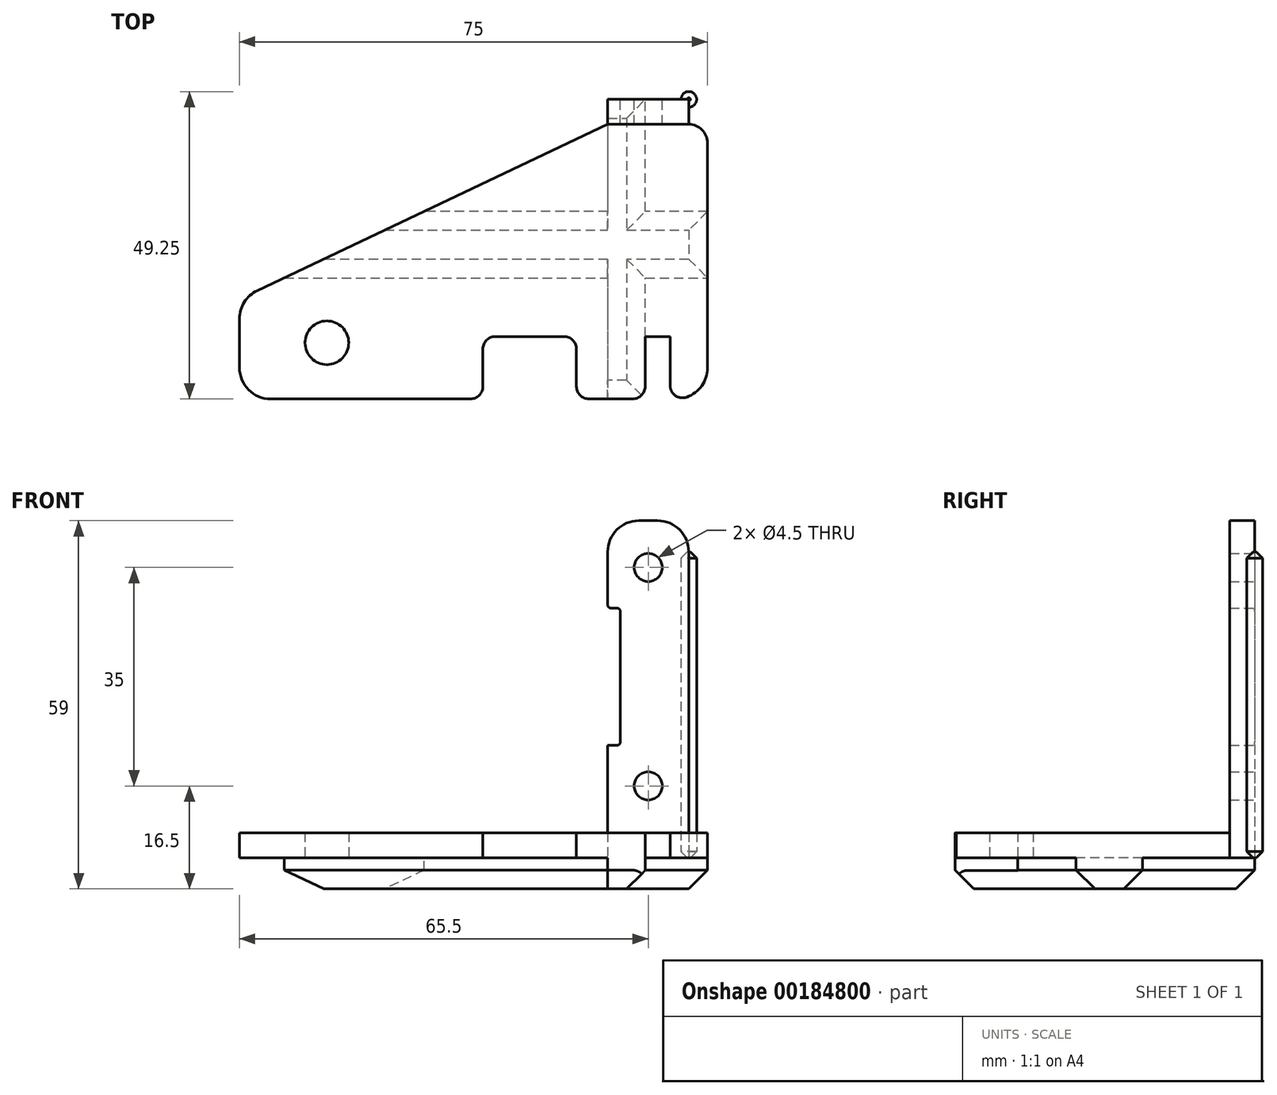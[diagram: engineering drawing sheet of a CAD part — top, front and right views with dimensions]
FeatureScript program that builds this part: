
annotation { "Feature Type Name" : "Feature", "Feature Type Description" : "" }
export const myFeature = defineFeature(function(context is Context, id is Id, definition is map)
    precondition{}
    {
        {
            var Q0;
            Q0=qCreatedBy(makeId("Top.planeOp"),FACE);
            var sketch = newSketch(context, id + "F0", { "sketchPlane" : qUnion([Q0])});
            skLineSegment(sketch, "E0.bottom", {"start": v(5, 0) * mm, "end": v(70, 0) * mm});
            skLineSegment(sketch, "E0.top", {"start": v(59, 44) * mm, "end": v(72, 44) * mm});
            skLineSegment(sketch, "E0.left", {"start": v(0, 5) * mm, "end": v(0, 12.84) * mm});
            skLineSegment(sketch, "E0.right", {"start": v(75, 5) * mm, "end": v(75, 41) * mm});
            skCircle(sketch, "E1", {"center": v(14, 9) * mm, "radius": 3.5 * mm});
            skLineSegment(sketch, "E2.bottom", {"start": v(69, 0) * mm, "end": v(65, 0) * mm});
            skLineSegment(sketch, "E2.top", {"start": v(69, 10) * mm, "end": v(65, 10) * mm});
            skLineSegment(sketch, "E2.left", {"start": v(69, 0) * mm, "end": v(69, 10) * mm});
            skLineSegment(sketch, "E2.right", {"start": v(65, 0) * mm, "end": v(65, 10) * mm});
            skLineSegment(sketch, "E3.bottom", {"start": v(72, 48) * mm, "end": v(59, 48) * mm});
            skLineSegment(sketch, "E3.top", {"start": v(72, 44) * mm, "end": v(59, 44) * mm});
            skLineSegment(sketch, "E3.left", {"start": v(72, 48) * mm, "end": v(72, 44) * mm});
            skLineSegment(sketch, "E3.right", {"start": v(59, 48) * mm, "end": v(59, 44) * mm});
            skLineSegment(sketch, "E4", {"start": v(59, 44) * mm, "end": v(2.86, 17.36) * mm});
            skPoint(sketch, "E5.visualSharp", {"position": v(75, 44) * mm});
            skArc(sketch, "E5.filletArc", {"start": v(75, 41) * mm, "mid": v(74.12, 43.12) * mm, "end": v(72, 44) * mm});
            skPoint(sketch, "E6.visualSharp", {"position": v(75, 0) * mm});
            skArc(sketch, "E6.filletArc", {"start": v(70, 0) * mm, "mid": v(73.54, 1.46) * mm, "end": v(75, 5) * mm});
            skPoint(sketch, "E7.visualSharp", {"position": v(0, 16) * mm});
            skArc(sketch, "E7.filletArc", {"start": v(2.86, 17.36) * mm, "mid": v(0.77, 15.51) * mm, "end": v(0, 12.84) * mm});
            skPoint(sketch, "E8.visualSharp", {"position": v(0, 0) * mm});
            skArc(sketch, "E8.filletArc", {"start": v(0, 5) * mm, "mid": v(1.46, 1.46) * mm, "end": v(5, 0) * mm});
            skLineSegment(sketch, "E9.bottom", {"start": v(39, 0) * mm, "end": v(54, 0) * mm});
            skLineSegment(sketch, "E9.top", {"start": v(39, 10) * mm, "end": v(54, 10) * mm});
            skLineSegment(sketch, "E9.left", {"start": v(39, 0) * mm, "end": v(39, 10) * mm});
            skLineSegment(sketch, "E9.right", {"start": v(54, 0) * mm, "end": v(54, 10) * mm});
            skSolve(sketch);
        }
        {
            var Q0;
            Q0=makeQuery(id+"F0.imprint","IMPRINT",FACE,{"disambiguationData":[TD([[makeQuery(id+"F0.imprint","IMPRINT",EDGE,{"derivedFrom":sQuery(id+"F0.wireOp",EDGE,"E0.left")}),-1.0]])]});
            extrude(context, id + "F1", {"entities" : qUnion([Q0]), "depth" : 4 * mm});
        }
        {
            var Q0;
            Q0=makeQuery(id+"F0.imprint","IMPRINT",FACE,{"disambiguationData":[TD([[makeQuery(id+"F0.imprint","IMPRINT",EDGE,{"derivedFrom":sQuery(id+"F0.wireOp",EDGE,"E3.bottom")}),1.0]])]});
            extrude(context, id + "F2", {"entities" : qUnion([Q0]), "operationType" : NewBodyOperationType.ADD, "depth" : 54 * mm});
        }
        {
            var Q0;
            Q0=makeQuery(id+"F2.opExtrude","CAP_EDGE",EDGE,{"disambiguationData":[OSD([sQuery(id+"F0.wireOp",EDGE,"E3.left")])],"isStart":false});
            var Q1;
            Q1=makeQuery(id+"F2.opExtrude","CAP_EDGE",EDGE,{"disambiguationData":[OSD([sQuery(id+"F0.wireOp",EDGE,"E3.right")])],"isStart":false});
            fillet(context, id + "F3", {"entities" : qUnion([Q0, Q1]), "radius" : 5 * mm, "tangentPropagation" : true, "allowEdgeOverflow" : false});
        }
        {
            var Q0;
            Q0=makeQuery(id+"F0.imprint","IMPRINT",FACE,{"disambiguationData":[TD([[makeQuery(id+"F0.imprint","IMPRINT",EDGE,{"derivedFrom":sQuery(id+"F0.wireOp",EDGE,"E0.left")}),-1.0]])]});
            var sketch = newSketch(context, id + "F4", { "sketchPlane" : qUnion([Q0])});
            skLineSegment(sketch, "E10", {"start": v(7.19, 19.4) * mm, "end": v(59, 19.4) * mm});
            skLineSegment(sketch, "E11", {"start": v(75.05, 19.4) * mm, "end": v(75.05, 30.04) * mm});
            skLineSegment(sketch, "E12", {"start": v(75.05, 30.04) * mm, "end": v(65.04, 30.04) * mm});
            skLineSegment(sketch, "E13", {"start": v(29.59, 30.04) * mm, "end": v(7.19, 19.4) * mm});
            skLineSegment(sketch, "E14", {"start": v(59, 48) * mm, "end": v(59, 30.04) * mm});
            skLineSegment(sketch, "E15", {"start": v(59, 0) * mm, "end": v(65.04, 0) * mm});
            skLineSegment(sketch, "E16", {"start": v(65.04, 0) * mm, "end": v(65.04, 19.4) * mm});
            skLineSegment(sketch, "E17", {"start": v(65.04, 48) * mm, "end": v(59, 48) * mm});
            skLineSegment(sketch, "E18.trimOffspring", {"start": v(59, 19.4) * mm, "end": v(59, 0) * mm});
            skLineSegment(sketch, "E19.trimOffspring", {"start": v(65.04, 30.04) * mm, "end": v(65.04, 48) * mm});
            skLineSegment(sketch, "E20.trimOffspring", {"start": v(65.04, 19.4) * mm, "end": v(75.05, 19.4) * mm});
            skLineSegment(sketch, "E21.trimOffspring", {"start": v(59, 30.04) * mm, "end": v(29.59, 30.04) * mm});
            skCircle(sketch, "E22", {"center": v(72, 48) * mm, "radius": 1.25 * mm});
            skSolve(sketch);
        }
        {
            var Q0;
            {var subQ24=sQuery(id+"F4.wireOp",EDGE,"E10");Q0=makeQuery(id+"F4.imprint","IMPRINT",FACE,{"disambiguationData":[TD([[makeQuery(id+"F4.imprint","IMPRINT",EDGE,{"derivedFrom":subQ24}),1.0]])]});}
            var Q1;
            {var subQ0=sQuery(id+"F4.wireOp",EDGE,"E17");Q1=makeQuery(id+"F4.imprint","IMPRINT",FACE,{"disambiguationData":[TD([[makeQuery(id+"F4.imprint","IMPRINT",EDGE,{"derivedFrom":subQ0}),1.0]])]});}
            extrude(context, id + "F5", {"entities" : qUnion([Q0, Q1]), "operationType" : NewBodyOperationType.ADD, "oppositeDirection" : true, "depth" : 5 * mm});
        }
        {
            var Q0;
            Q0=makeQuery(id+"F5.opExtrude","CAP_EDGE",EDGE,{"disambiguationData":[OSD([sQuery(id+"F4.wireOp",EDGE,"E17")])],"isStart":false});
            var Q1;
            Q1=makeQuery(id+"F5.opExtrude","CAP_EDGE",EDGE,{"disambiguationData":[OSD([sQuery(id+"F4.wireOp",EDGE,"E15")])],"isStart":false});
            var Q2;
            Q2=makeQuery(id+"F5.opExtrude","CAP_EDGE",EDGE,{"disambiguationData":[OSD([sQuery(id+"F0.wireOp",EDGE,"E0.right")])],"isStart":false});
            var Q3;
            Q3=makeQuery(id+"F5.opExtrude","CAP_EDGE",EDGE,{"disambiguationData":[OSD([sQuery(id+"F4.wireOp",EDGE,"E12")])],"isStart":false});
            var Q4;
            Q4=makeQuery(id+"F5.opExtrude","CAP_EDGE",EDGE,{"disambiguationData":[OSD([sQuery(id+"F4.wireOp",EDGE,"E20.trimOffspring")])],"isStart":false});
            var Q5;
            Q5=makeQuery(id+"F5.opExtrude","CAP_EDGE",EDGE,{"disambiguationData":[OSD([sQuery(id+"F4.wireOp",EDGE,"E19.trimOffspring")])],"isStart":false});
            var Q6;
            Q6=makeQuery(id+"F5.opExtrude","CAP_EDGE",EDGE,{"disambiguationData":[OSD([sQuery(id+"F4.wireOp",EDGE,"E21.trimOffspring")])],"isStart":false});
            var Q7;
            Q7=makeQuery(id+"F5.opExtrude","CAP_EDGE",EDGE,{"disambiguationData":[OSD([sQuery(id+"F0.wireOp",EDGE,"E4")])],"isStart":false});
            var Q8;
            Q8=makeQuery(id+"F5.opExtrude","CAP_EDGE",EDGE,{"disambiguationData":[OSD([sQuery(id+"F4.wireOp",EDGE,"E10")])],"isStart":false});
            var Q9;
            Q9=makeQuery(id+"F5.opExtrude","CAP_EDGE",EDGE,{"disambiguationData":[OSD([sQuery(id+"F4.wireOp",EDGE,"E16")])],"isStart":false});
            chamfer(context, id + "F6", {"entities" : qUnion([Q0, Q1, Q2, Q3, Q4, Q5, Q6, Q7, Q8, Q9]), "width" : 3 * mm, "tangentPropagation" : true});
        }
        {
            var Q0;
            Q0=makeQuery(id+"F4.imprint","IMPRINT",FACE,{"disambiguationData":[TD([[makeQuery(id+"F4.imprint","IMPRINT",EDGE,{"derivedFrom":sQuery(id+"F4.wireOp",EDGE,"E22")}),1.0]])]});
            extrude(context, id + "F7", {"entities" : qUnion([Q0]), "operationType" : NewBodyOperationType.ADD, "depth" : 49 * mm});
        }
        {
            var Q0;
            Q0=makeQuery(id+"F7.opExtrude","CAP_EDGE",EDGE,{"disambiguationData":[OSD([sQuery(id+"F4.wireOp",EDGE,"E22")])],"isStart":false});
            chamfer(context, id + "F8", {"entities" : qUnion([Q0]), "width" : 1 * mm, "tangentPropagation" : true});
        }
        {
            var Q0;
            Q0=makeQuery(id+"F7.opExtrude","CAP_EDGE",EDGE,{"disambiguationData":[OSD([sQuery(id+"F4.wireOp",EDGE,"E22")])],"isStart":true});
            chamfer(context, id + "F9", {"entities" : qUnion([Q0]), "width" : 1 * mm, "tangentPropagation" : true});
        }
        {
            var Q0;
            Q0=makeQuery(id+"F5.boolean.opBoolean","MERGE",FACE,{"derivedFrom":[makeQuery(id+"F2.opExtrude","SWEPT_FACE",FACE,{"disambiguationData":[OSD([sQuery(id+"F0.wireOp",EDGE,"E3.bottom")])]}),makeQuery(id+"F5.opExtrude","SWEPT_FACE",FACE,{"disambiguationData":[OSD([sQuery(id+"F4.wireOp",EDGE,"E17")])]})]});
            var sketch = newSketch(context, id + "F10", { "sketchPlane" : qUnion([Q0])});
            skCircle(sketch, "E23", {"center": v(-65.5, 46.5) * mm, "radius": 2.25 * mm});
            skCircle(sketch, "E24", {"center": v(-65.5, 11.5) * mm, "radius": 2.25 * mm});
            skSolve(sketch);
        }
        {
            var Q0;
            Q0=makeQuery(id+"F10.imprint","IMPRINT",FACE,{"disambiguationData":[TD([[makeQuery(id+"F10.imprint","IMPRINT",EDGE,{"derivedFrom":sQuery(id+"F10.wireOp",EDGE,"E24")}),1.0]])]});
            var Q1;
            Q1=makeQuery(id+"F10.imprint","IMPRINT",FACE,{"disambiguationData":[TD([[makeQuery(id+"F10.imprint","IMPRINT",EDGE,{"derivedFrom":sQuery(id+"F10.wireOp",EDGE,"E23")}),1.0]])]});
            extrude(context, id + "F11", {"entities" : qUnion([Q0, Q1]), "operationType" : NewBodyOperationType.REMOVE, "oppositeDirection" : true, "depth" : 5 * mm});
        }
        {
            var Q0;
            Q0=makeQuery(id+"F1.opExtrude","SWEPT_EDGE",EDGE,{"disambiguationData":[OSD([sQuery(id+"F0.wireOp",EDGE,"E9.top"),sQuery(id+"F0.wireOp",EDGE,"E9.right")])]});
            var Q1;
            Q1=makeQuery(id+"F1.opExtrude","SWEPT_EDGE",EDGE,{"disambiguationData":[OSD([sQuery(id+"F0.wireOp",EDGE,"E0.bottom"),sQuery(id+"F0.wireOp",EDGE,"E9.bottom"),sQuery(id+"F0.wireOp",EDGE,"E9.right")])]});
            var Q2;
            Q2=makeQuery(id+"F1.opExtrude","SWEPT_EDGE",EDGE,{"disambiguationData":[OSD([sQuery(id+"F0.wireOp",EDGE,"E9.top"),sQuery(id+"F0.wireOp",EDGE,"E9.left")])]});
            var Q3;
            Q3=makeQuery(id+"F1.opExtrude","SWEPT_EDGE",EDGE,{"disambiguationData":[OSD([sQuery(id+"F0.wireOp",EDGE,"E0.bottom"),sQuery(id+"F0.wireOp",EDGE,"E9.bottom"),sQuery(id+"F0.wireOp",EDGE,"E9.left")])]});
            var Q4;
            {var subQ0=sQuery(id+"F0.wireOp",EDGE,"E2.right");Q4=makeQuery(id+"F5.boolean.opBoolean","MERGE",EDGE,{"derivedFrom":[makeQuery(id+"F1.opExtrude","SWEPT_EDGE",EDGE,{"disambiguationData":[OSD([sQuery(id+"F0.wireOp",EDGE,"E0.bottom"),sQuery(id+"F0.wireOp",EDGE,"E2.bottom"),subQ0])]}),makeQuery(id+"F5.opExtrude","SWEPT_EDGE",EDGE,{"disambiguationData":[OSD([subQ0,sQuery(id+"F4.wireOp",EDGE,"E15")])]})]});}
            var Q5;
            Q5=makeQuery(id+"F1.opExtrude","SWEPT_EDGE",EDGE,{"disambiguationData":[OSD([sQuery(id+"F0.wireOp",EDGE,"E0.bottom"),sQuery(id+"F0.wireOp",EDGE,"E2.bottom"),sQuery(id+"F0.wireOp",EDGE,"E2.left")])]});
            fillet(context, id + "F12", {"entities" : qUnion([Q0, Q1, Q2, Q3, Q4, Q5]), "radius" : 2 * mm, "tangentPropagation" : true, "allowEdgeOverflow" : false});
        }
        {
            var Q0;
            Q0=makeQuery(id+"F5.boolean.opBoolean","MERGE",FACE,{"derivedFrom":[makeQuery(id+"F2.opExtrude","SWEPT_FACE",FACE,{"disambiguationData":[OSD([sQuery(id+"F0.wireOp",EDGE,"E3.bottom")])]}),makeQuery(id+"F5.opExtrude","SWEPT_FACE",FACE,{"disambiguationData":[OSD([sQuery(id+"F4.wireOp",EDGE,"E17")])]})]});
            var sketch = newSketch(context, id + "F13", { "sketchPlane" : qUnion([Q0])});
            skLineSegment(sketch, "E25.bottom", {"start": v(-61, 40) * mm, "end": v(-59, 40) * mm});
            skLineSegment(sketch, "E25.top", {"start": v(-61, 18) * mm, "end": v(-59, 18) * mm});
            skLineSegment(sketch, "E25.left", {"start": v(-61, 40) * mm, "end": v(-61, 18) * mm});
            skLineSegment(sketch, "E25.right", {"start": v(-59, 40) * mm, "end": v(-59, 18) * mm});
            skSolve(sketch);
        }
        {
            var Q0;
            Q0 = qSketchRegion(id + "F13", true);
            extrude(context, id + "F14", {"entities" : qUnion([Q0]), "operationType" : NewBodyOperationType.REMOVE, "oppositeDirection" : true, "depth" : 5 * mm});
        }
        {
            var Q0;
            Q0=makeQuery(id+"F14.boolean.opBoolean","COPY",EDGE,{"derivedFrom":makeQuery(id+"F14.opExtrude","SWEPT_EDGE",EDGE,{"disambiguationData":[OSD([sQuery(id+"F0.wireOp",EDGE,"E3.bottom"),sQuery(id+"F0.wireOp",EDGE,"E3.right"),sQuery(id+"F4.wireOp",EDGE,"E14"),sQuery(id+"F4.wireOp",EDGE,"E17"),sQuery(id+"F13.wireOp",EDGE,"E25.bottom"),sQuery(id+"F13.wireOp",EDGE,"E25.right")])]})});
            var Q1;
            Q1=makeQuery(id+"F14.boolean.opBoolean","COPY",EDGE,{"derivedFrom":makeQuery(id+"F14.opExtrude","SWEPT_EDGE",EDGE,{"disambiguationData":[OSD([sQuery(id+"F0.wireOp",EDGE,"E3.bottom"),sQuery(id+"F0.wireOp",EDGE,"E3.right"),sQuery(id+"F4.wireOp",EDGE,"E14"),sQuery(id+"F4.wireOp",EDGE,"E17"),sQuery(id+"F13.wireOp",EDGE,"E25.top"),sQuery(id+"F13.wireOp",EDGE,"E25.right")])]})});
            var Q2;
            Q2=makeQuery(id+"F14.boolean.opBoolean","COPY",EDGE,{"derivedFrom":makeQuery(id+"F14.opExtrude","SWEPT_EDGE",EDGE,{"disambiguationData":[OSD([sQuery(id+"F13.wireOp",EDGE,"E25.top"),sQuery(id+"F13.wireOp",EDGE,"E25.left")])]})});
            var Q3;
            Q3=makeQuery(id+"F14.boolean.opBoolean","COPY",EDGE,{"derivedFrom":makeQuery(id+"F14.opExtrude","SWEPT_EDGE",EDGE,{"disambiguationData":[OSD([sQuery(id+"F13.wireOp",EDGE,"E25.bottom"),sQuery(id+"F13.wireOp",EDGE,"E25.left")])]})});
            fillet(context, id + "F15", {"entities" : qUnion([Q0, Q1, Q2, Q3]), "radius" : 0.5 * mm, "tangentPropagation" : true, "allowEdgeOverflow" : false});
        }
    });
